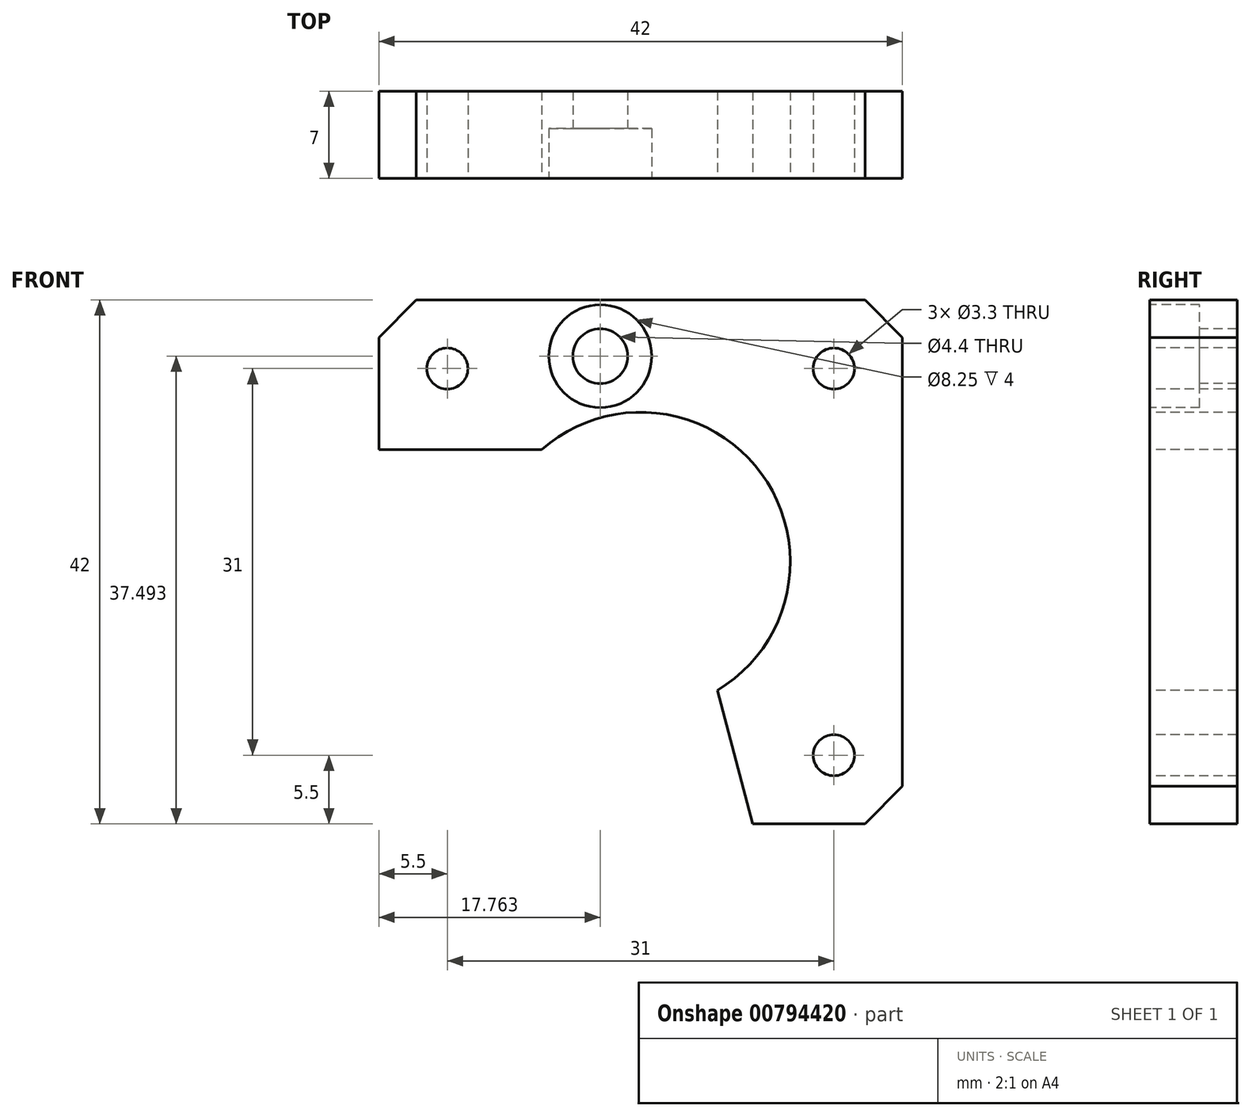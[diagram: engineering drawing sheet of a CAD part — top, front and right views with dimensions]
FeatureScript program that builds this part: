
annotation { "Feature Type Name" : "Feature", "Feature Type Description" : "" }
export const myFeature = defineFeature(function(context is Context, id is Id, definition is map)
    precondition{}
    {
        {
            var Q0;
            Q0=qCreatedBy(makeId("Front.planeOp"),FACE);
            var sketch = newSketch(context, id + "F0", { "sketchPlane" : qUnion([Q0])});
            skLineSegment(sketch, "E0.bottom", {"start": v(0, 0) * mm, "end": v(42, 0) * mm});
            skLineSegment(sketch, "E0.top", {"start": v(0, 42) * mm, "end": v(42, 42) * mm});
            skLineSegment(sketch, "E0.left", {"start": v(0, 0) * mm, "end": v(0, 42) * mm});
            skLineSegment(sketch, "E0.right", {"start": v(42, 0) * mm, "end": v(42, 42) * mm});
            skSolve(sketch);
        }
        {
            var Q0;
            Q0=makeQuery(id+"F0.imprint","IMPRINT",FACE,{"disambiguationData":[TD([[makeQuery(id+"F0.imprint","IMPRINT",EDGE,{"derivedFrom":sQuery(id+"F0.wireOp",EDGE,"E0.bottom")}),1.0]])]});
            extrude(context, id + "F1", {"entities" : qUnion([Q0]), "depth" : 7 * mm, "offsetDistance" : 25 * mm});
        }
        {
            var Q0;
            Q0=makeQuery(id+"F1.opExtrude","CAP_FACE",FACE,{"disambiguationData":[OSD([sQuery(id+"F0.wireOp",EDGE,"E0.bottom"),sQuery(id+"F0.wireOp",EDGE,"E0.top"),sQuery(id+"F0.wireOp",EDGE,"E0.left"),sQuery(id+"F0.wireOp",EDGE,"E0.right")])],"isStart":false});
            var sketch = newSketch(context, id + "F2", { "sketchPlane" : qUnion([Q0])});
            skCircle(sketch, "E1", {"center": v(21, 21) * mm, "radius": 12 * mm});
            skPoint(sketch, "E1.centerSnap0", {"position": v(42, 21) * mm});
            skPoint(sketch, "E1.centerSnap1", {"position": v(21, 0) * mm});
            skSolve(sketch);
        }
        {
            var Q0;
            Q0=makeQuery(id+"F2.imprint","IMPRINT",FACE,{"disambiguationData":[TD([[makeQuery(id+"F2.imprint","IMPRINT",EDGE,{"derivedFrom":sQuery(id+"F2.wireOp",EDGE,"E1")}),1.0]])]});
            extrude(context, id + "F3", {"entities" : qUnion([Q0]), "operationType" : NewBodyOperationType.REMOVE, "oppositeDirection" : true, "depth" : 25 * mm, "offsetDistance" : 25 * mm});
        }
        {
            var Q0;
            Q0=makeQuery(id+"F1.opExtrude","CAP_FACE",FACE,{"disambiguationData":[OSD([sQuery(id+"F0.wireOp",EDGE,"E0.bottom"),sQuery(id+"F0.wireOp",EDGE,"E0.top"),sQuery(id+"F0.wireOp",EDGE,"E0.left"),sQuery(id+"F0.wireOp",EDGE,"E0.right")])],"isStart":false});
            var sketch = newSketch(context, id + "F4", { "sketchPlane" : qUnion([Q0])});
            skLineSegment(sketch, "E2", {"start": v(0, 30) * mm, "end": v(22.02, 30) * mm});
            skLineSegment(sketch, "E3", {"start": v(22.02, 30) * mm, "end": v(30, 0) * mm});
            skLineSegment(sketch, "E4", {"start": v(30, 0) * mm, "end": v(0, 0) * mm});
            skLineSegment(sketch, "E5", {"start": v(0, 0) * mm, "end": v(0, 30) * mm});
            skSolve(sketch);
        }
        {
            var Q0;
            {var subQ0=sQuery(id+"F4.wireOp",EDGE,"E4");Q0=makeQuery(id+"F4.imprint","IMPRINT",FACE,{"disambiguationData":[TD([[makeQuery(id+"F4.imprint","IMPRINT",EDGE,{"derivedFrom":subQ0}),1.0]])]});}
            var Q1;
            {var subQ0=sQuery(id+"F4.wireOp",EDGE,"E3");var subQ1=sQuery(id+"F4.wireOp",EDGE,"E2");var subQ2=makeQuery(id+"F4.imprint","INTERSECT",VERTEX,{"derivedFrom":[subQ1,subQ0]});Q1=makeQuery(id+"F4.imprint","IMPRINT",FACE,{"disambiguationData":[TD([[makeQuery(id+"F4.imprint","IMPRINT",EDGE,{"disambiguationData":[TD([[subQ2,1.0]])],"derivedFrom":subQ1}),-1.0]])]});}
            extrude(context, id + "F5", {"entities" : qUnion([Q0, Q1]), "operationType" : NewBodyOperationType.REMOVE, "oppositeDirection" : true, "depth" : 25 * mm, "offsetDistance" : 25 * mm});
        }
        {
            var Q0;
            Q0=makeQuery(id+"F1.opExtrude","CAP_FACE",FACE,{"disambiguationData":[OSD([sQuery(id+"F0.wireOp",EDGE,"E0.bottom"),sQuery(id+"F0.wireOp",EDGE,"E0.top"),sQuery(id+"F0.wireOp",EDGE,"E0.left"),sQuery(id+"F0.wireOp",EDGE,"E0.right")])],"isStart":false});
            var sketch = newSketch(context, id + "F6", { "sketchPlane" : qUnion([Q0])});
            skPoint(sketch, "E6", {"position": v(5.5, 36.5) * mm});
            skPoint(sketch, "E7", {"position": v(36.5, 36.5) * mm});
            skPoint(sketch, "E8", {"position": v(36.5, 5.5) * mm});
            skSolve(sketch);
        }
        {
            var Q0;
            Q0=sQuery(id+"F6.wireOp",VERTEX,"E6");
            var Q1;
            Q1=sQuery(id+"F6.wireOp",VERTEX,"E7");
            var Q2;
            Q2=sQuery(id+"F6.wireOp",VERTEX,"E8");
            var Q3;
            Q3=makeQuery(id+"F1.opExtrude","SWEPT_BODY",BODY,{"disambiguationData":[OSD([sQuery(id+"F0.wireOp",EDGE,"E0.bottom"),sQuery(id+"F0.wireOp",EDGE,"E0.top"),sQuery(id+"F0.wireOp",EDGE,"E0.left"),sQuery(id+"F0.wireOp",EDGE,"E0.right")])]});
            hole(context, id + "F7", {"style" : HoleStyle.SIMPLE, "endStyle" : HoleEndStyle.BLIND, "standardTappedOrClearance" : lookupTablePath({ "standard" : "ISO", "fit" : "Normal", "size" : "M3", "type" : "Clearance" }), "standardBlindInLast" : lookupTablePath({ "fit" : "Standard", "standard" : "ISO", "size" : "M3", "type" : "Clearance" }), "holeDiameter" : 3.3 * mm, "majorDiameter" : 3 * mm, "holeDepth" : 13.5 * mm, "isTappedThrough" : true, "tappedDepth" : 12 * mm, "tapClearance" : 3, "locations" : qUnion([Q0, Q1, Q2]), "scope" : qUnion([Q3])});
        }
        {
            var Q0;
            Q0=makeQuery(id+"F1.opExtrude","SWEPT_EDGE",EDGE,{"disambiguationData":[OSD([sQuery(id+"F0.wireOp",EDGE,"E0.top"),sQuery(id+"F0.wireOp",EDGE,"E0.left")])]});
            var Q1;
            Q1=makeQuery(id+"F1.opExtrude","SWEPT_EDGE",EDGE,{"disambiguationData":[OSD([sQuery(id+"F0.wireOp",EDGE,"E0.top"),sQuery(id+"F0.wireOp",EDGE,"E0.right")])]});
            var Q2;
            Q2=makeQuery(id+"F1.opExtrude","SWEPT_EDGE",EDGE,{"disambiguationData":[OSD([sQuery(id+"F0.wireOp",EDGE,"E0.bottom"),sQuery(id+"F0.wireOp",EDGE,"E0.right")])]});
            chamfer(context, id + "F8", {"entities" : qUnion([Q0, Q1, Q2]), "width" : 3 * mm, "tangentPropagation" : true});
        }
        {
            var Q0;
            Q0=makeQuery(id+"F1.opExtrude","CAP_FACE",FACE,{"disambiguationData":[OSD([sQuery(id+"F0.wireOp",EDGE,"E0.bottom"),sQuery(id+"F0.wireOp",EDGE,"E0.top"),sQuery(id+"F0.wireOp",EDGE,"E0.left"),sQuery(id+"F0.wireOp",EDGE,"E0.right")])],"isStart":false});
            var sketch = newSketch(context, id + "F9", { "sketchPlane" : qUnion([Q0])});
            skPoint(sketch, "E9", {"position": v(17.76, 37.5) * mm});
            skSolve(sketch);
        }
        {
            var Q0;
            Q0=sQuery(id+"F9.wireOp",VERTEX,"E9");
            var Q1;
            Q1=makeQuery(id+"F1.opExtrude","SWEPT_BODY",BODY,{"disambiguationData":[OSD([sQuery(id+"F0.wireOp",EDGE,"E0.bottom"),sQuery(id+"F0.wireOp",EDGE,"E0.top"),sQuery(id+"F0.wireOp",EDGE,"E0.left"),sQuery(id+"F0.wireOp",EDGE,"E0.right")])]});
            hole(context, id + "F10", {"style" : HoleStyle.C_BORE, "endStyle" : HoleEndStyle.THROUGH, "standardTappedOrClearance" : lookupTablePath({ "fit" : "Standard", "standard" : "ISO", "size" : "M4", "type" : "Clearance" }), "standardBlindInLast" : lookupTablePath({ "fit" : "Standard", "standard" : "ISO", "size" : "M4", "type" : "Clearance" }), "holeDiameter" : 4.4 * mm, "cBoreDiameter" : 8.25 * mm, "cBoreDepth" : 4 * mm, "majorDiameter" : 5 * mm, "isTappedThrough" : true, "tappedDepth" : 12 * mm, "tapClearance" : 3, "locations" : qUnion([Q0]), "scope" : qUnion([Q1])});
        }
    });
